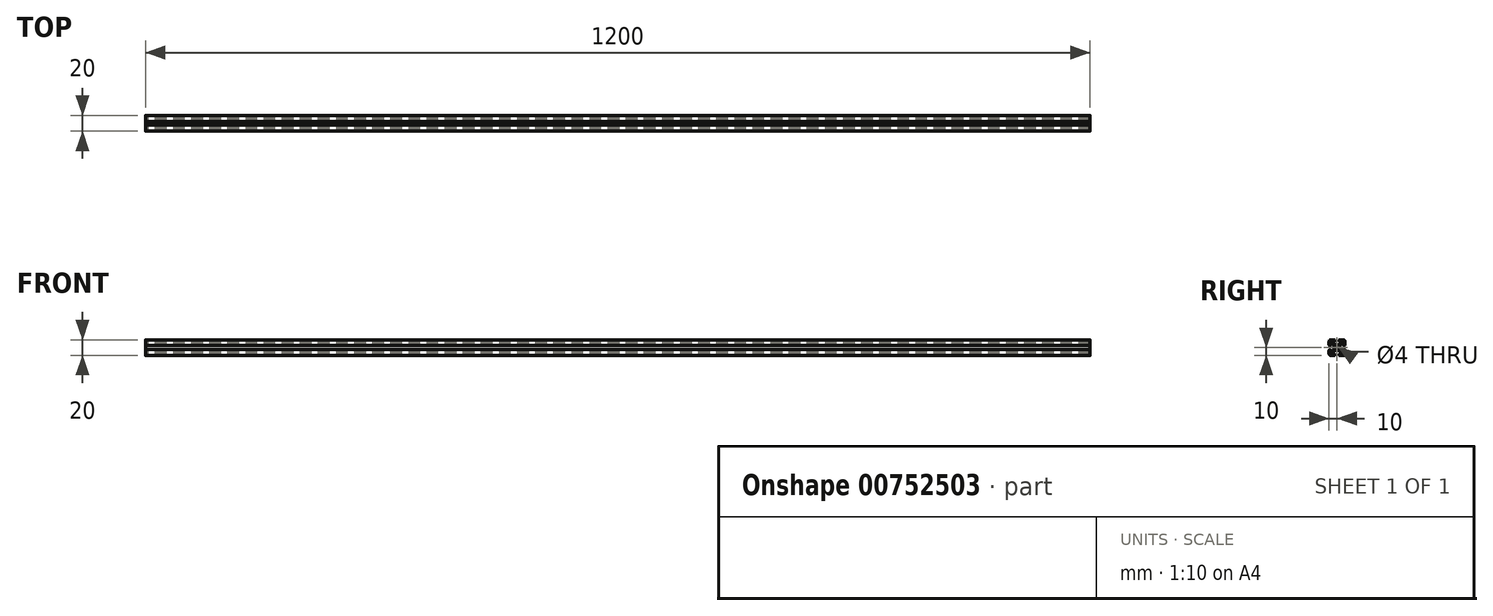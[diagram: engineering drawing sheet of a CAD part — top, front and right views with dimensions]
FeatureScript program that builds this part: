
annotation { "Feature Type Name" : "Feature", "Feature Type Description" : "" }
export const myFeature = defineFeature(function(context is Context, id is Id, definition is map)
    precondition{}
    {
        {
            var Q0;
            Q0=qCreatedBy(makeId("Right.planeOp"),FACE);
            var sketch = newSketch(context, id + "F0", { "sketchPlane" : qUnion([Q0])});
            skLineSegment(sketch, "E0.bottom", {"start": v(-8, 10) * mm, "end": v(-3.3, 10) * mm});
            skLineSegment(sketch, "E0.top", {"start": v(-8, -10) * mm, "end": v(-3.3, -10) * mm});
            skLineSegment(sketch, "E0.right", {"start": v(10, 8) * mm, "end": v(10, 3.3) * mm});
            skLineSegment(sketch, "E1", {"start": v(0, 31.7) * mm, "end": v(0, -24.01) * mm, "construction": true});
            skLineSegment(sketch, "E2", {"start": v(-29.71, 0) * mm, "end": v(21.95, 0) * mm, "construction": true});
            skLineSegment(sketch, "E3", {"start": v(-2.5, 9.2) * mm, "end": v(-2.5, 8.5) * mm});
            skLineSegment(sketch, "E4", {"start": v(-2.8, 8.2) * mm, "end": v(-4.92, 8.2) * mm});
            skLineSegment(sketch, "E5", {"start": v(-5.5, 6.78) * mm, "end": v(-3.25, 4.53) * mm});
            skLineSegment(sketch, "E6", {"start": v(-1.13, 3.65) * mm, "end": v(1.14, 3.65) * mm});
            skLineSegment(sketch, "E7", {"start": v(3.25, 4.53) * mm, "end": v(5.5, 6.78) * mm});
            skLineSegment(sketch, "E8", {"start": v(4.92, 8.2) * mm, "end": v(2.8, 8.2) * mm});
            skLineSegment(sketch, "E9", {"start": v(2.5, 8.5) * mm, "end": v(2.5, 9.2) * mm});
            skLineSegment(sketch, "E10.trimOffspring", {"start": v(3.3, 10) * mm, "end": v(8, 10) * mm});
            skArc(sketch, "E11.filletArc", {"start": v(-8, 10) * mm, "mid": v(-9.41, 9.41) * mm, "end": v(-10, 8) * mm});
            skArc(sketch, "E12.filletArc", {"start": v(-10, -8) * mm, "mid": v(-9.41, -9.41) * mm, "end": v(-8, -10) * mm});
            skArc(sketch, "E13.filletArc", {"start": v(8, -10) * mm, "mid": v(9.41, -9.41) * mm, "end": v(10, -8) * mm});
            skArc(sketch, "E14.filletArc", {"start": v(10, 8) * mm, "mid": v(9.41, 9.41) * mm, "end": v(8, 10) * mm});
            skPoint(sketch, "E15.visualSharp", {"position": v(-9.03, 10.3) * mm});
            skArc(sketch, "E15.filletArc", {"start": v(-4.92, 8.2) * mm, "mid": v(-5.69, 7.69) * mm, "end": v(-5.5, 6.78) * mm});
            skPoint(sketch, "E16.visualSharp", {"position": v(-2.37, 3.65) * mm});
            skArc(sketch, "E16.filletArc", {"start": v(-3.25, 4.53) * mm, "mid": v(-2.28, 3.88) * mm, "end": v(-1.13, 3.65) * mm});
            skPoint(sketch, "E17.visualSharp", {"position": v(2.37, 3.65) * mm});
            skArc(sketch, "E17.filletArc", {"start": v(1.14, 3.65) * mm, "mid": v(2.28, 3.88) * mm, "end": v(3.25, 4.53) * mm});
            skArc(sketch, "E18.filletArc", {"start": v(5.5, 6.78) * mm, "mid": v(5.69, 7.69) * mm, "end": v(4.92, 8.2) * mm});
            skPoint(sketch, "E19.visualSharp", {"position": v(2.5, 8.2) * mm});
            skArc(sketch, "E19.filletArc", {"start": v(2.5, 8.5) * mm, "mid": v(2.59, 8.29) * mm, "end": v(2.8, 8.2) * mm});
            skPoint(sketch, "E20.visualSharp", {"position": v(-2.5, 8.2) * mm});
            skArc(sketch, "E20.filletArc", {"start": v(-2.8, 8.2) * mm, "mid": v(-2.59, 8.29) * mm, "end": v(-2.5, 8.5) * mm});
            skPoint(sketch, "E21.1.5", {"position": v(-3.65, 2.37) * mm});
            skPoint(sketch, "E21.1.13", {"position": v(-10.3, 9.03) * mm});
            skPoint(sketch, "E21.center", {"position": v(0, 0) * mm});
            skLineSegment(sketch, "E22.trimOffspring", {"start": v(-10, -3.3) * mm, "end": v(-10, -8) * mm});
            skLineSegment(sketch, "E23.trimOffspring", {"start": v(10, -3.3) * mm, "end": v(10, -8) * mm});
            skLineSegment(sketch, "E24.trimOffspring", {"start": v(3.3, -10) * mm, "end": v(8, -10) * mm});
            skLineSegment(sketch, "E25", {"start": v(-10, 8) * mm, "end": v(-10, 3.3) * mm});
            skCircle(sketch, "E26", {"center": v(0, 0) * mm, "radius": 2 * mm});
            skPoint(sketch, "E27.visualSharp", {"position": v(-2.5, 10) * mm});
            skArc(sketch, "E27.filletArc", {"start": v(-2.5, 9.2) * mm, "mid": v(-2.73, 9.77) * mm, "end": v(-3.3, 10) * mm});
            skPoint(sketch, "E28.visualSharp", {"position": v(2.5, 10) * mm});
            skArc(sketch, "E28.filletArc", {"start": v(3.3, 10) * mm, "mid": v(2.73, 9.77) * mm, "end": v(2.5, 9.2) * mm});
            skPoint(sketch, "E29.1.1", {"position": v(-10, -2.5) * mm});
            skLineSegment(sketch, "E29.1.2", {"start": v(-3.65, -1.13) * mm, "end": v(-3.65, 1.14) * mm});
            skArc(sketch, "E29.1.3", {"start": v(-4.53, -3.25) * mm, "mid": v(-3.88, -2.28) * mm, "end": v(-3.65, -1.13) * mm});
            skPoint(sketch, "E29.1.4", {"position": v(-8.2, -2.5) * mm});
            skArc(sketch, "E29.1.5", {"start": v(-8.2, -4.92) * mm, "mid": v(-7.69, -5.69) * mm, "end": v(-6.78, -5.5) * mm});
            skLineSegment(sketch, "E29.1.6", {"start": v(-8.2, -2.8) * mm, "end": v(-8.2, -4.92) * mm});
            skLineSegment(sketch, "E29.1.7", {"start": v(-8.2, 4.92) * mm, "end": v(-8.2, 2.8) * mm});
            skArc(sketch, "E29.1.8", {"start": v(-3.65, 1.14) * mm, "mid": v(-3.88, 2.28) * mm, "end": v(-4.53, 3.25) * mm});
            skArc(sketch, "E29.1.9", {"start": v(-6.78, 5.5) * mm, "mid": v(-7.69, 5.69) * mm, "end": v(-8.2, 4.92) * mm});
            skPoint(sketch, "E29.1.10", {"position": v(-3.65, -2.37) * mm});
            skPoint(sketch, "E29.1.11", {"position": v(-10, 2.5) * mm});
            skPoint(sketch, "E29.1.12", {"position": v(-8.2, 2.5) * mm});
            skLineSegment(sketch, "E29.1.13", {"start": v(-6.78, -5.5) * mm, "end": v(-4.53, -3.25) * mm});
            skLineSegment(sketch, "E29.1.14", {"start": v(-4.53, 3.25) * mm, "end": v(-6.78, 5.5) * mm});
            skArc(sketch, "E29.1.15", {"start": v(-10, 3.3) * mm, "mid": v(-9.77, 2.73) * mm, "end": v(-9.2, 2.5) * mm});
            skArc(sketch, "E29.1.16", {"start": v(-9.2, -2.5) * mm, "mid": v(-9.77, -2.73) * mm, "end": v(-10, -3.3) * mm});
            skLineSegment(sketch, "E29.1.17", {"start": v(-8.5, 2.5) * mm, "end": v(-9.2, 2.5) * mm});
            skLineSegment(sketch, "E29.1.18", {"start": v(-9.2, -2.5) * mm, "end": v(-8.5, -2.5) * mm});
            skArc(sketch, "E29.1.19", {"start": v(-8.2, -2.8) * mm, "mid": v(-8.29, -2.59) * mm, "end": v(-8.5, -2.5) * mm});
            skArc(sketch, "E29.1.20", {"start": v(-8.5, 2.5) * mm, "mid": v(-8.29, 2.59) * mm, "end": v(-8.2, 2.8) * mm});
            skPoint(sketch, "E29.2.0", {"position": v(-2.37, -3.65) * mm});
            skPoint(sketch, "E29.2.1", {"position": v(2.5, -10) * mm});
            skLineSegment(sketch, "E29.2.2", {"start": v(1.13, -3.65) * mm, "end": v(-1.14, -3.65) * mm});
            skArc(sketch, "E29.2.3", {"start": v(3.25, -4.53) * mm, "mid": v(2.28, -3.88) * mm, "end": v(1.13, -3.65) * mm});
            skPoint(sketch, "E29.2.4", {"position": v(2.5, -8.2) * mm});
            skArc(sketch, "E29.2.5", {"start": v(4.92, -8.2) * mm, "mid": v(5.69, -7.69) * mm, "end": v(5.5, -6.78) * mm});
            skLineSegment(sketch, "E29.2.6", {"start": v(2.8, -8.2) * mm, "end": v(4.92, -8.2) * mm});
            skLineSegment(sketch, "E29.2.7", {"start": v(-4.92, -8.2) * mm, "end": v(-2.8, -8.2) * mm});
            skArc(sketch, "E29.2.8", {"start": v(-1.14, -3.65) * mm, "mid": v(-2.28, -3.88) * mm, "end": v(-3.25, -4.53) * mm});
            skArc(sketch, "E29.2.9", {"start": v(-5.5, -6.78) * mm, "mid": v(-5.69, -7.69) * mm, "end": v(-4.92, -8.2) * mm});
            skPoint(sketch, "E29.2.10", {"position": v(2.37, -3.65) * mm});
            skPoint(sketch, "E29.2.11", {"position": v(-2.5, -10) * mm});
            skPoint(sketch, "E29.2.12", {"position": v(-2.5, -8.2) * mm});
            skLineSegment(sketch, "E29.2.13", {"start": v(5.5, -6.78) * mm, "end": v(3.25, -4.53) * mm});
            skLineSegment(sketch, "E29.2.14", {"start": v(-3.25, -4.53) * mm, "end": v(-5.5, -6.78) * mm});
            skArc(sketch, "E29.2.15", {"start": v(-3.3, -10) * mm, "mid": v(-2.73, -9.77) * mm, "end": v(-2.5, -9.2) * mm});
            skArc(sketch, "E29.2.16", {"start": v(2.5, -9.2) * mm, "mid": v(2.73, -9.77) * mm, "end": v(3.3, -10) * mm});
            skLineSegment(sketch, "E29.2.17", {"start": v(-2.5, -8.5) * mm, "end": v(-2.5, -9.2) * mm});
            skLineSegment(sketch, "E29.2.18", {"start": v(2.5, -9.2) * mm, "end": v(2.5, -8.5) * mm});
            skArc(sketch, "E29.2.19", {"start": v(2.8, -8.2) * mm, "mid": v(2.59, -8.29) * mm, "end": v(2.5, -8.5) * mm});
            skArc(sketch, "E29.2.20", {"start": v(-2.5, -8.5) * mm, "mid": v(-2.59, -8.29) * mm, "end": v(-2.8, -8.2) * mm});
            skPoint(sketch, "E29.3.0", {"position": v(3.65, -2.37) * mm});
            skPoint(sketch, "E29.3.1", {"position": v(10, 2.5) * mm});
            skLineSegment(sketch, "E29.3.2", {"start": v(3.65, 1.13) * mm, "end": v(3.65, -1.14) * mm});
            skArc(sketch, "E29.3.3", {"start": v(4.53, 3.25) * mm, "mid": v(3.88, 2.28) * mm, "end": v(3.65, 1.13) * mm});
            skPoint(sketch, "E29.3.4", {"position": v(8.2, 2.5) * mm});
            skArc(sketch, "E29.3.5", {"start": v(8.2, 4.92) * mm, "mid": v(7.69, 5.69) * mm, "end": v(6.78, 5.5) * mm});
            skLineSegment(sketch, "E29.3.6", {"start": v(8.2, 2.8) * mm, "end": v(8.2, 4.92) * mm});
            skLineSegment(sketch, "E29.3.7", {"start": v(8.2, -4.92) * mm, "end": v(8.2, -2.8) * mm});
            skArc(sketch, "E29.3.8", {"start": v(3.65, -1.14) * mm, "mid": v(3.88, -2.28) * mm, "end": v(4.53, -3.25) * mm});
            skArc(sketch, "E29.3.9", {"start": v(6.78, -5.5) * mm, "mid": v(7.69, -5.69) * mm, "end": v(8.2, -4.92) * mm});
            skPoint(sketch, "E29.3.10", {"position": v(3.65, 2.37) * mm});
            skPoint(sketch, "E29.3.11", {"position": v(10, -2.5) * mm});
            skPoint(sketch, "E29.3.12", {"position": v(8.2, -2.5) * mm});
            skLineSegment(sketch, "E29.3.13", {"start": v(6.78, 5.5) * mm, "end": v(4.53, 3.25) * mm});
            skLineSegment(sketch, "E29.3.14", {"start": v(4.53, -3.25) * mm, "end": v(6.78, -5.5) * mm});
            skArc(sketch, "E29.3.15", {"start": v(10, -3.3) * mm, "mid": v(9.77, -2.73) * mm, "end": v(9.2, -2.5) * mm});
            skArc(sketch, "E29.3.16", {"start": v(9.2, 2.5) * mm, "mid": v(9.77, 2.73) * mm, "end": v(10, 3.3) * mm});
            skLineSegment(sketch, "E29.3.17", {"start": v(8.5, -2.5) * mm, "end": v(9.2, -2.5) * mm});
            skLineSegment(sketch, "E29.3.18", {"start": v(9.2, 2.5) * mm, "end": v(8.5, 2.5) * mm});
            skArc(sketch, "E29.3.19", {"start": v(8.2, 2.8) * mm, "mid": v(8.29, 2.59) * mm, "end": v(8.5, 2.5) * mm});
            skArc(sketch, "E29.3.20", {"start": v(8.5, -2.5) * mm, "mid": v(8.29, -2.59) * mm, "end": v(8.2, -2.8) * mm});
            skSolve(sketch);
        }
        {
            var Q0;
            Q0=qSketchRegion(id+"F0",true);
            extrude(context, id + "F1", {"entities" : qUnion([Q0]), "depth" : 1200 * mm, "offsetDistance" : 25 * mm});
        }
    });
